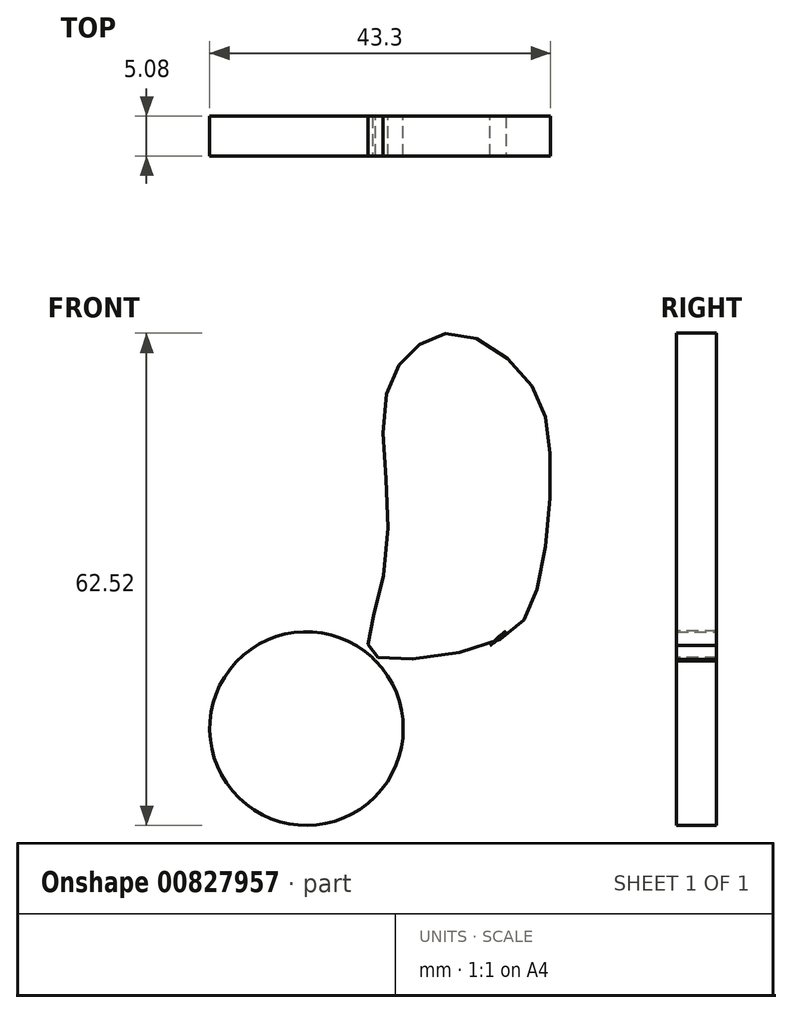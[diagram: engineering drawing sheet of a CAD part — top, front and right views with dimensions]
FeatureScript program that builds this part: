
annotation { "Feature Type Name" : "Feature", "Feature Type Description" : "" }
export const myFeature = defineFeature(function(context is Context, id is Id, definition is map)
    precondition{}
    {
        {
            var Q0;
            Q0=qCreatedBy(makeId("Front.planeOp"),FACE);
            var sketch = newSketch(context, id + "F0", { "sketchPlane" : qUnion([Q0])});
            skCircle(sketch, "E0", {"center": v(-56.46, 21.54) * mm, "radius": 12.3 * mm});
            skCircle(sketch, "E1", {"center": v(-22.64, 22.74) * mm, "radius": 14.03 * mm});
            skFitSpline(sketch, "E2", {"points": [v(-48.1, 30.54) * mm, v(-46.2, 44.48) * mm, v(-44.99, 68.03) * mm, v(-30.9, 68.84) * mm, v(-31.1, 33.94) * mm, v(-48.1, 30.54) * mm]});
            skFitSpline(sketch, "E3", {"points": [v(-46.67, 61.82) * mm, v(-38.14, 62) * mm, v(-28.78, 66.03) * mm, v(-46.67, 61.82) * mm]});
            skCircle(sketch, "E4", {"center": v(-38.55, 68.44) * mm, "radius": 1.4 * mm});
            skSolve(sketch);
        }
        {
            var Q0;
            Q0=qCreatedBy(makeId("Front.planeOp"),FACE);
            var sketch = newSketch(context, id + "F1", { "sketchPlane" : qUnion([Q0])});
            skFitSpline(sketch, "E5", {"points": [v(-47.4, 30.6) * mm, v(-48.6, 32.4) * mm, v(-46.2, 44.48) * mm, v(-46.6, 62.4) * mm, v(-42.97, 69.64) * mm, v(-36.73, 71.66) * mm, v(-28.08, 65.42) * mm, v(-25.46, 55.35) * mm, v(-27.48, 38.24) * mm, v(-32.9, 32.4) * mm, v(-47.4, 30.6) * mm]});
            skSolve(sketch);
        }
        {
            var Q0;
            {var subQ0=sQuery(id+"F0.wireOp",EDGE,"E2");var subQ1=sQuery(id+"F0.wireOp",EDGE,"E0");var subQ2=makeQuery(id+"F0.imprint","INTERSECT",VERTEX,{"disambiguationData":[OD(0.0)],"derivedFrom":[subQ1,subQ0]});Q0=makeQuery(id+"F0.imprint","IMPRINT",FACE,{"disambiguationData":[TD([[makeQuery(id+"F0.imprint","IMPRINT",EDGE,{"disambiguationData":[TD([[subQ2,-1.0]])],"derivedFrom":subQ1}),1.0]])]});}
            var Q1;
            Q1=makeQuery(id+"F1.imprint","IMPRINT",FACE,{"disambiguationData":[TD([[makeQuery(id+"F1.imprint","IMPRINT",EDGE,{"derivedFrom":sQuery(id+"F1.wireOp",EDGE,"E5")}),-1.0]])]});
            var Q2;
            {var subQ0=sQuery(id+"F0.wireOp",EDGE,"E2");var subQ1=sQuery(id+"F0.wireOp",EDGE,"E1");var subQ2=makeQuery(id+"F0.imprint","INTERSECT",VERTEX,{"disambiguationData":[OD(0.0)],"derivedFrom":[subQ1,subQ0]});Q2=makeQuery(id+"F0.imprint","IMPRINT",FACE,{"disambiguationData":[TD([[makeQuery(id+"F0.imprint","IMPRINT",EDGE,{"disambiguationData":[TD([[subQ2,-1.0]])],"derivedFrom":subQ1}),1.0]])]});}
            extrude(context, id + "F2", {"entities" : qUnion([Q0, Q1, Q2]), "depth" : 5.08 * mm, "offsetDistance" : 25.4 * mm});
        }
    });
